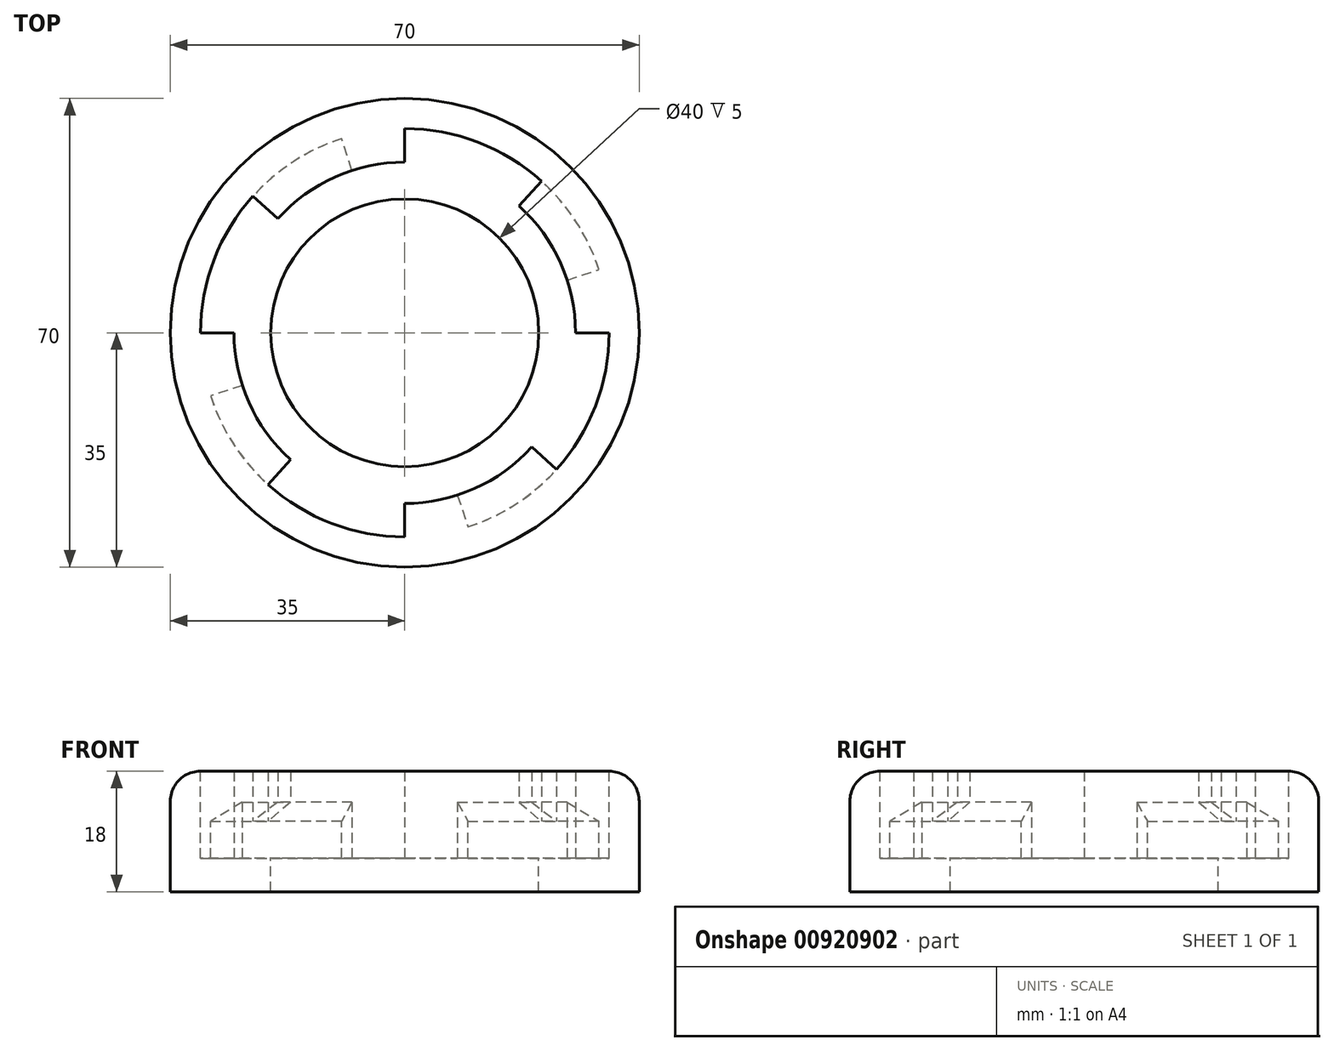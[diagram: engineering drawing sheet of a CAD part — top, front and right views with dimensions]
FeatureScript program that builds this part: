
annotation { "Feature Type Name" : "Feature", "Feature Type Description" : "" }
export const myFeature = defineFeature(function(context is Context, id is Id, definition is map)
    precondition{}
    {
        {
            var Q0;
            Q0=qCreatedBy(makeId("Front.planeOp"),FACE);
            var sketch = newSketch(context, id + "F0", { "sketchPlane" : qUnion([Q0])});
            skLineSegment(sketch, "E0", {"start": v(17.5, 0) * mm, "end": v(17.5, 2) * mm});
            skLineSegment(sketch, "E1", {"start": v(17.5, 2) * mm, "end": v(20, 2) * mm});
            skLineSegment(sketch, "E2", {"start": v(20, 2) * mm, "end": v(20, 7) * mm});
            skLineSegment(sketch, "E3", {"start": v(20, 7) * mm, "end": v(30.5, 7) * mm});
            skLineSegment(sketch, "E4", {"start": v(30.5, 7) * mm, "end": v(30.5, 12.5) * mm});
            skLineSegment(sketch, "E5", {"start": v(30.5, 12.5) * mm, "end": v(25.5, 15.39) * mm});
            skLineSegment(sketch, "E6", {"start": v(25.5, 15.39) * mm, "end": v(25.5, 20) * mm});
            skLineSegment(sketch, "E7", {"start": v(25.5, 20) * mm, "end": v(35, 20) * mm});
            skLineSegment(sketch, "E8", {"start": v(35, 20) * mm, "end": v(35, 0) * mm});
            skLineSegment(sketch, "E9", {"start": v(35, 0) * mm, "end": v(17.5, 0) * mm});
            skSolve(sketch);
        }
        {
            var Q0;
            Q0=qCreatedBy(makeId("Front.planeOp"),FACE);
            var sketch = newSketch(context, id + "F1", { "sketchPlane" : qUnion([Q0])});
            skLineSegment(sketch, "E10", {"start": v(0, 47.14) * mm, "end": v(0, -19.48) * mm});
            skSolve(sketch);
        }
        {
            var Q0;
            Q0=makeQuery(id+"F0.imprint","IMPRINT",FACE,{"disambiguationData":[TD([[makeQuery(id+"F0.imprint","IMPRINT",EDGE,{"derivedFrom":sQuery(id+"F0.wireOp",EDGE,"E0")}),-1.0]])]});
            var Q1;
            Q1=sQuery(id+"F1.wireOp",EDGE,"E10");
            revolve(context, id + "F2", {"surfaceOperationType" : NewSurfaceOperationType.NEW, "entities" : qUnion([Q0]), "axis" : qUnion([Q1]), "revolveType" : RevolveType.FULL});
        }
        {
            var Q0;
            Q0=qCreatedBy(makeId("Top.planeOp"),FACE);
            var sketch = newSketch(context, id + "F3", { "sketchPlane" : qUnion([Q0])});
            skLineSegment(sketch, "E11", {"start": v(25.5, 0) * mm, "end": v(35, 0) * mm});
            skLineSegment(sketch, "E12", {"start": v(24.25, 7.88) * mm, "end": v(33.29, 10.82) * mm});
            skArc(sketch, "E13", {"start": v(25.5, 0) * mm, "mid": v(25.19, 3.99) * mm, "end": v(24.25, 7.88) * mm});
            skArc(sketch, "E14", {"start": v(35, 0) * mm, "mid": v(34.57, 5.48) * mm, "end": v(33.29, 10.82) * mm});
            skArc(sketch, "E15.1.0", {"start": v(0, 35) * mm, "mid": v(-5.48, 34.57) * mm, "end": v(-10.82, 33.29) * mm});
            skArc(sketch, "E15.1.1", {"start": v(0, 25.5) * mm, "mid": v(-3.99, 25.19) * mm, "end": v(-7.88, 24.25) * mm});
            skLineSegment(sketch, "E15.1.2", {"start": v(-7.88, 24.25) * mm, "end": v(-10.82, 33.29) * mm});
            skLineSegment(sketch, "E15.1.3", {"start": v(0, 25.5) * mm, "end": v(0, 35) * mm});
            skArc(sketch, "E15.2.0", {"start": v(-35, 0) * mm, "mid": v(-34.57, -5.48) * mm, "end": v(-33.29, -10.82) * mm});
            skArc(sketch, "E15.2.1", {"start": v(-25.5, 0) * mm, "mid": v(-25.19, -3.99) * mm, "end": v(-24.25, -7.88) * mm});
            skLineSegment(sketch, "E15.2.2", {"start": v(-24.25, -7.88) * mm, "end": v(-33.29, -10.82) * mm});
            skLineSegment(sketch, "E15.2.3", {"start": v(-25.5, 0) * mm, "end": v(-35, 0) * mm});
            skArc(sketch, "E15.3.0", {"start": v(0, -35) * mm, "mid": v(5.48, -34.57) * mm, "end": v(10.82, -33.29) * mm});
            skArc(sketch, "E15.3.1", {"start": v(0, -25.5) * mm, "mid": v(3.99, -25.19) * mm, "end": v(7.88, -24.25) * mm});
            skLineSegment(sketch, "E15.3.2", {"start": v(7.88, -24.25) * mm, "end": v(10.82, -33.29) * mm});
            skLineSegment(sketch, "E15.3.3", {"start": v(0, -25.5) * mm, "end": v(0, -35) * mm});
            skSolve(sketch);
        }
        {
            var Q0;
            Q0 = qSketchRegion(id + "F3", true);
            var Q1;
            Q1=makeQuery(id+"F2.opRevolve","SWEPT_FACE",FACE,{"disambiguationData":[OSD([sQuery(id+"F0.wireOp",EDGE,"E7")])]});
            extrude(context, id + "F4", {"entities" : qUnion([Q0]), "operationType" : NewBodyOperationType.ADD, "endBound" : BoundingType.UP_TO_SURFACE, "depth" : 25 * mm, "endBoundEntityFace" : qUnion([Q1]), "offsetDistance" : 25 * mm});
        }
        {
            var Q0;
            Q0=qCreatedBy(makeId("Top.planeOp"),FACE);
            var sketch = newSketch(context, id + "F5", { "sketchPlane" : qUnion([Q0])});
            skLineSegment(sketch, "E16", {"start": v(0, 25.5) * mm, "end": v(0, 30.5) * mm});
            skLineSegment(sketch, "E17", {"start": v(17.06, 18.95) * mm, "end": v(20.4, 22.67) * mm});
            skArc(sketch, "E18", {"start": v(17.06, 18.95) * mm, "mid": v(9.14, 23.8) * mm, "end": v(0, 25.5) * mm});
            skArc(sketch, "E19", {"start": v(20.4, 22.67) * mm, "mid": v(10.93, 28.47) * mm, "end": v(0, 30.5) * mm});
            skArc(sketch, "E20.1.0", {"start": v(-18.95, 17.06) * mm, "mid": v(-23.8, 9.14) * mm, "end": v(-25.5, 0) * mm});
            skArc(sketch, "E20.1.1", {"start": v(-22.67, 20.4) * mm, "mid": v(-28.47, 10.93) * mm, "end": v(-30.5, 0) * mm});
            skLineSegment(sketch, "E20.1.2", {"start": v(-18.95, 17.06) * mm, "end": v(-22.67, 20.4) * mm});
            skLineSegment(sketch, "E20.1.3", {"start": v(-25.5, 0) * mm, "end": v(-30.5, 0) * mm});
            skArc(sketch, "E20.2.0", {"start": v(-17.06, -18.95) * mm, "mid": v(-9.14, -23.8) * mm, "end": v(0, -25.5) * mm});
            skArc(sketch, "E20.2.1", {"start": v(-20.4, -22.67) * mm, "mid": v(-10.93, -28.47) * mm, "end": v(0, -30.5) * mm});
            skLineSegment(sketch, "E20.2.2", {"start": v(-17.06, -18.95) * mm, "end": v(-20.4, -22.67) * mm});
            skLineSegment(sketch, "E20.2.3", {"start": v(0, -25.5) * mm, "end": v(0, -30.5) * mm});
            skArc(sketch, "E20.3.0", {"start": v(18.95, -17.06) * mm, "mid": v(23.8, -9.14) * mm, "end": v(25.5, 0) * mm});
            skArc(sketch, "E20.3.1", {"start": v(22.67, -20.4) * mm, "mid": v(28.47, -10.93) * mm, "end": v(30.5, 0) * mm});
            skLineSegment(sketch, "E20.3.2", {"start": v(18.95, -17.06) * mm, "end": v(22.67, -20.4) * mm});
            skLineSegment(sketch, "E20.3.3", {"start": v(25.5, 0) * mm, "end": v(30.5, 0) * mm});
            skSolve(sketch);
        }
        {
            var Q0;
            Q0 = qSketchRegion(id + "F5", true);
            var Q1;
            Q1=makeQuery(id+"F2.opRevolve","SWEPT_FACE",FACE,{"disambiguationData":[OSD([sQuery(id+"F0.wireOp",EDGE,"E7")])]});
            var Q2;
            Q2=makeQuery(id+"F2.opRevolve","SWEPT_FACE",FACE,{"disambiguationData":[OSD([sQuery(id+"F0.wireOp",EDGE,"E3")])]});
            extrude(context, id + "F6", {"entities" : qUnion([Q0]), "operationType" : NewBodyOperationType.REMOVE, "endBound" : BoundingType.UP_TO_SURFACE, "depth" : 25 * mm, "endBoundEntityFace" : qUnion([Q1]), "offsetDistance" : 25 * mm, "hasSecondDirection" : true, "secondDirectionBound" : SecondDirectionBoundingType.UP_TO_SURFACE, "secondDirectionOppositeDirection" : false, "secondDirectionDepth" : 25 * mm, "secondDirectionBoundEntityFace" : qUnion([Q2])});
        }
        {
            var Q0;
            Q0=makeQuery(id+"F2.opRevolve","SWEPT_FACE",FACE,{"disambiguationData":[OSD([sQuery(id+"F0.wireOp",EDGE,"E9")])]});
            var sketch = newSketch(context, id + "F7", { "sketchPlane" : qUnion([Q0])});
            skCircle(sketch, "E21", {"center": v(0, 0) * mm, "radius": 35 * mm});
            skSolve(sketch);
        }
        {
            var Q0;
            Q0 = qSketchRegion(id + "F7", true);
            extrude(context, id + "F8", {"entities" : qUnion([Q0]), "operationType" : NewBodyOperationType.REMOVE, "oppositeDirection" : true, "depth" : 2 * mm, "offsetDistance" : 25 * mm});
        }
        {
            var Q0;
            Q0=makeQuery(id+"F2.opRevolve","SWEPT_EDGE",EDGE,{"disambiguationData":[OSD([sQuery(id+"F0.wireOp",EDGE,"E7"),sQuery(id+"F0.wireOp",EDGE,"E8")])]});
            fillet(context, id + "F9", {"entities" : qUnion([Q0]), "radius" : 4.5 * mm, "tangentPropagation" : true, "allowEdgeOverflow" : false});
        }
    });
